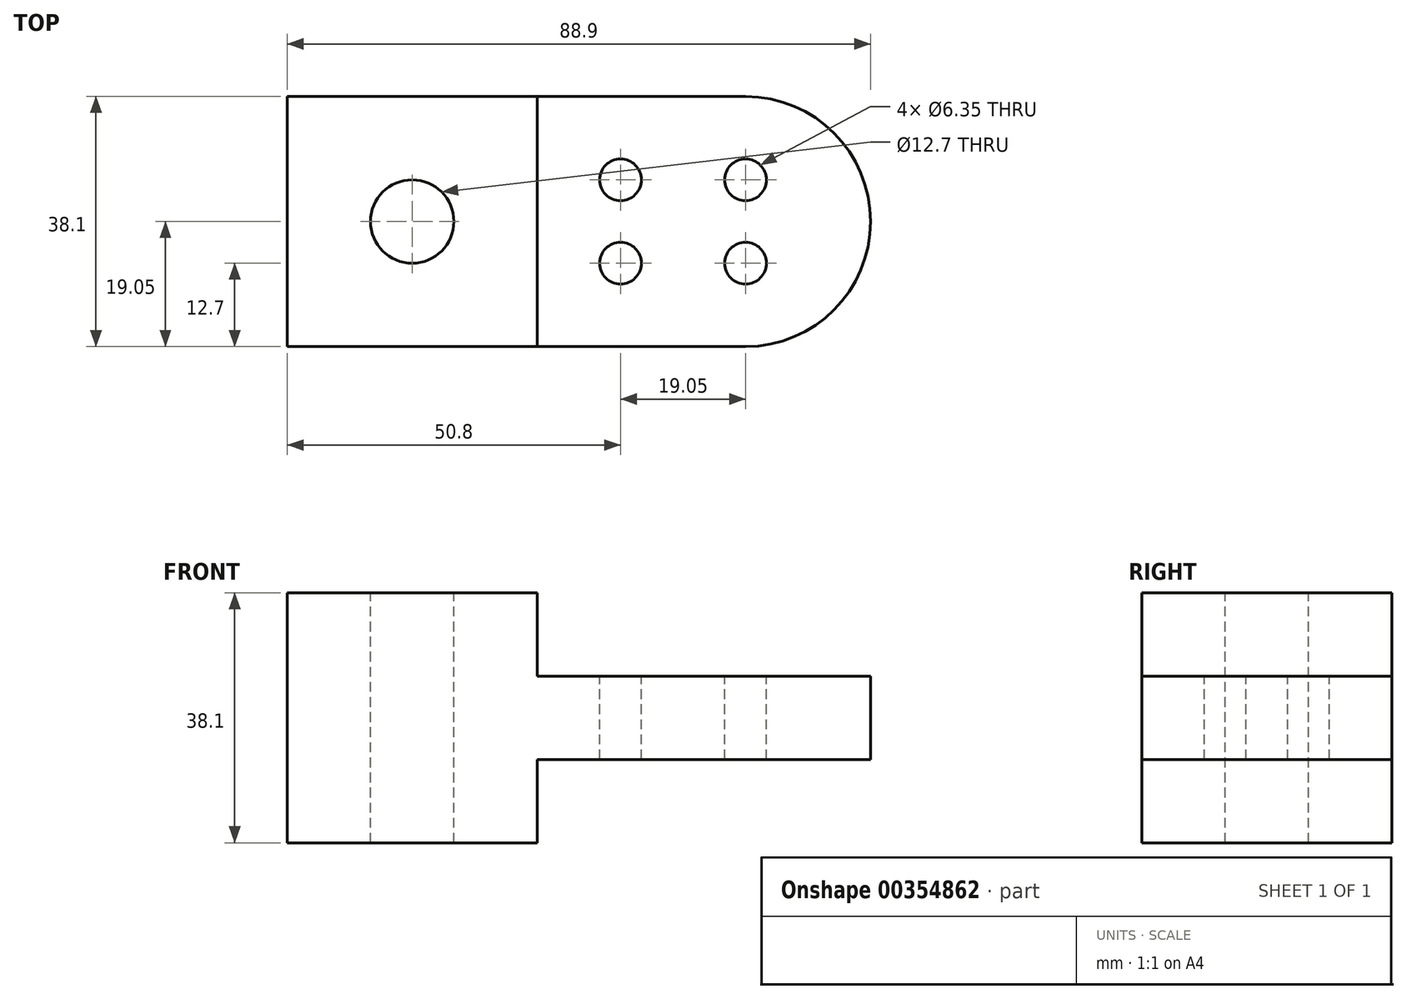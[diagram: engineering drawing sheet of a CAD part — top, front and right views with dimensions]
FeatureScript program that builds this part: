
annotation { "Feature Type Name" : "Feature", "Feature Type Description" : "" }
export const myFeature = defineFeature(function(context is Context, id is Id, definition is map)
    precondition{}
    {
        {
            var Q0;
            Q0=qCreatedBy(makeId("Front.planeOp"),FACE);
            var sketch = newSketch(context, id + "F0", { "sketchPlane" : qUnion([Q0])});
            skLineSegment(sketch, "E0.bottom", {"start": v(-19.05, 19.05) * mm, "end": v(19.05, 19.05) * mm});
            skLineSegment(sketch, "E0.top", {"start": v(-19.05, -19.05) * mm, "end": v(19.05, -19.05) * mm});
            skLineSegment(sketch, "E0.left", {"start": v(-19.05, 19.05) * mm, "end": v(-19.05, -19.05) * mm});
            skLineSegment(sketch, "E0.right", {"start": v(19.05, 19.05) * mm, "end": v(19.05, 6.35) * mm});
            skLineSegment(sketch, "E1.bottom", {"start": v(19.05, 6.35) * mm, "end": v(69.85, 6.35) * mm});
            skLineSegment(sketch, "E1.top", {"start": v(19.05, -6.35) * mm, "end": v(69.85, -6.35) * mm});
            skLineSegment(sketch, "E1.right", {"start": v(69.85, 6.35) * mm, "end": v(69.85, -6.35) * mm});
            skLineSegment(sketch, "E2.trimOffspring", {"start": v(19.05, -6.35) * mm, "end": v(19.05, -19.05) * mm});
            skSolve(sketch);
        }
        {
            var Q0;
            Q0 = qSketchRegion(id + "F0", true);
            extrude(context, id + "F1", {"entities" : qUnion([Q0]), "depth" : 38.1 * mm});
        }
        {
            var Q0;
            Q0=makeQuery(id+"F1.opExtrude","SWEPT_FACE",FACE,{"disambiguationData":[OSD([sQuery(id+"F0.wireOp",EDGE,"E0.bottom")])]});
            var sketch = newSketch(context, id + "F2", { "sketchPlane" : qUnion([Q0])});
            skCircle(sketch, "E3", {"center": v(0, -19.05) * mm, "radius": 6.35 * mm});
            skPoint(sketch, "E3.centerSnap0", {"position": v(19.05, -19.05) * mm});
            skCircle(sketch, "E4", {"center": v(31.75, -12.7) * mm, "radius": 3.18 * mm});
            skCircle(sketch, "E5", {"center": v(31.75, -25.4) * mm, "radius": 3.18 * mm});
            skCircle(sketch, "E6", {"center": v(50.8, -12.7) * mm, "radius": 3.18 * mm});
            skCircle(sketch, "E7", {"center": v(50.8, -25.4) * mm, "radius": 3.18 * mm});
            skLineSegment(sketch, "E8", {"start": v(50.8, -12.7) * mm, "end": v(50.8, -47.13) * mm, "construction": true});
            skLineSegment(sketch, "E9", {"start": v(50.8, -47.13) * mm, "end": v(50.8, 6.25) * mm, "construction": true});
            skArc(sketch, "E10.trimOffspring", {"start": v(50.8, -38.1) * mm, "mid": v(69.85, -19.05) * mm, "end": v(50.8, 0) * mm});
            skLineSegment(sketch, "E11", {"start": v(50.8, -38.1) * mm, "end": v(69.85, -38.1) * mm});
            skLineSegment(sketch, "E12", {"start": v(69.85, -38.1) * mm, "end": v(69.85, 0) * mm});
            skLineSegment(sketch, "E13", {"start": v(69.85, 0) * mm, "end": v(50.8, 0) * mm});
            skSolve(sketch);
        }
        {
            var Q0;
            Q0 = qSketchRegion(id + "F2", true);
            extrude(context, id + "F3", {"entities" : qUnion([Q0]), "operationType" : NewBodyOperationType.REMOVE, "endBound" : BoundingType.THROUGH_ALL, "oppositeDirection" : true, "depth" : 25.4 * mm});
        }
    });
